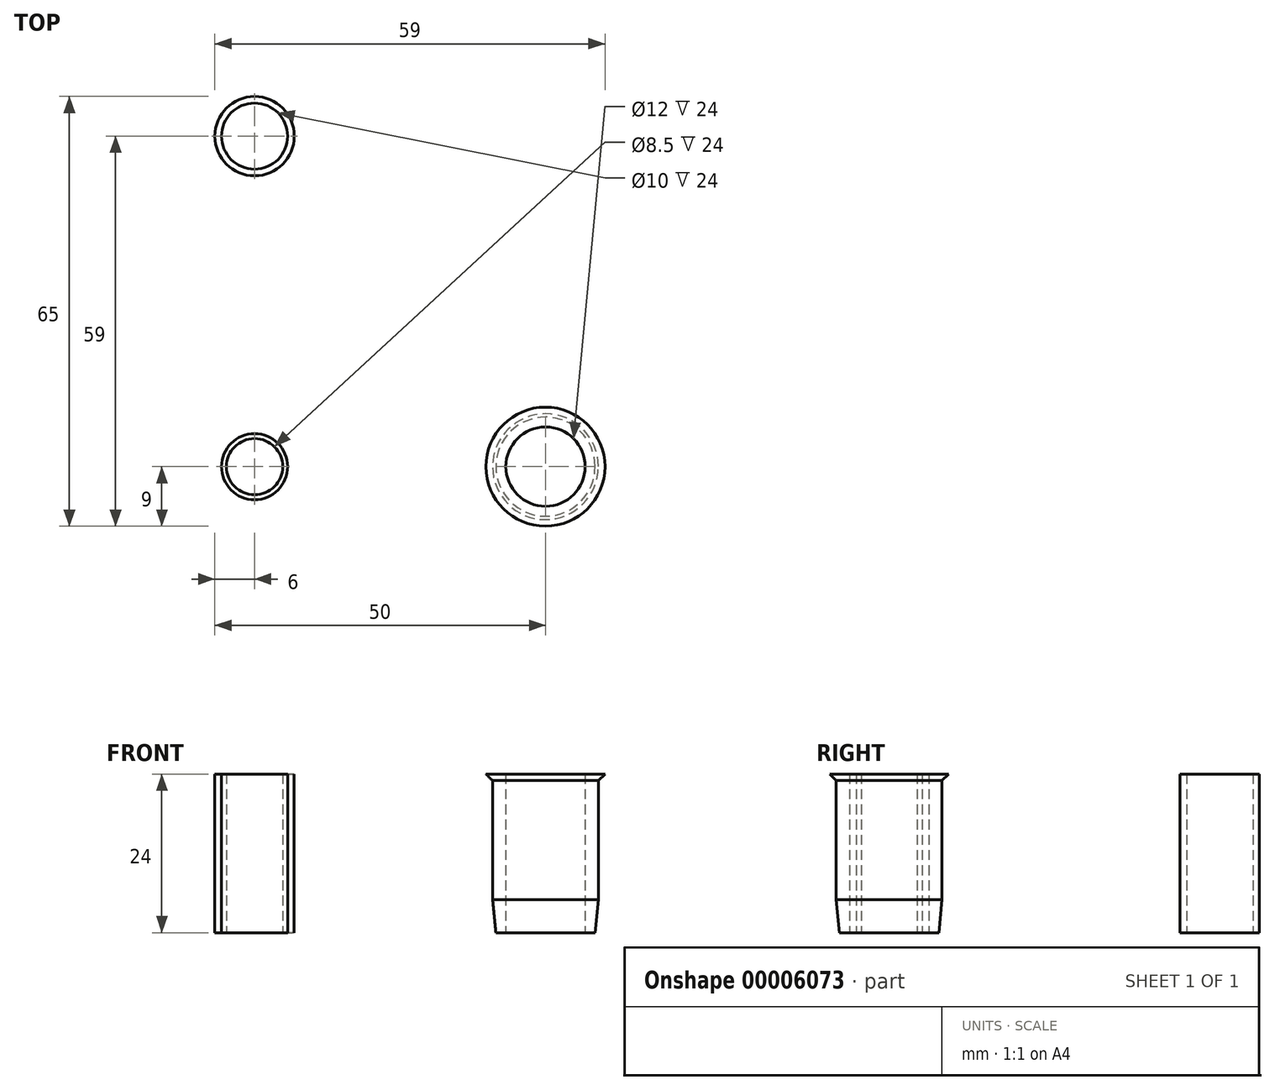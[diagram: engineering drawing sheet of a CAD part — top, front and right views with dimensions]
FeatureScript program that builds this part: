
annotation { "Feature Type Name" : "Feature", "Feature Type Description" : "" }
export const myFeature = defineFeature(function(context is Context, id is Id, definition is map)
    precondition{}
    {
        {
            var Q0;
            Q0=qCreatedBy(makeId("Top.planeOp"),FACE);
            var sketch = newSketch(context, id + "F0", { "sketchPlane" : qUnion([Q0])});
            skCircle(sketch, "E0", {"center": v(0, 0) * mm, "radius": 4.25 * mm});
            skCircle(sketch, "E1", {"center": v(0, 0) * mm, "radius": 5 * mm});
            skLineSegment(sketch, "E2.bottom", {"start": v(0, 0) * mm, "end": v(50, 0) * mm, "construction": true});
            skLineSegment(sketch, "E2.top", {"start": v(0, 50) * mm, "end": v(50, 50) * mm, "construction": true});
            skLineSegment(sketch, "E2.left", {"start": v(0, 0) * mm, "end": v(0, 50) * mm, "construction": true});
            skLineSegment(sketch, "E2.right", {"start": v(50, 0) * mm, "end": v(50, 50) * mm, "construction": true});
            skCircle(sketch, "E3", {"center": v(0, 50) * mm, "radius": 5 * mm});
            skCircle(sketch, "E4", {"center": v(0, 50) * mm, "radius": 6 * mm});
            skLineSegment(sketch, "E5.bottom", {"start": v(50, 0) * mm, "end": v(52, 0) * mm});
            skLineSegment(sketch, "E5.top", {"start": v(50, 24) * mm, "end": v(52, 24) * mm});
            skLineSegment(sketch, "E5.left", {"start": v(50, 0) * mm, "end": v(50, 24) * mm});
            skLineSegment(sketch, "E5.right", {"start": v(52, 0) * mm, "end": v(52, 24) * mm});
            skLineSegment(sketch, "E6", {"start": v(52, 24) * mm, "end": v(53, 24) * mm});
            skLineSegment(sketch, "E7", {"start": v(53, 24) * mm, "end": v(52, 23) * mm});
            skLineSegment(sketch, "E8", {"start": v(52, 23) * mm, "end": v(52, 24) * mm});
            skSolve(sketch);
        }
        {
            var Q0;
            Q0=makeQuery(id+"F0.imprint","IMPRINT",FACE,{"disambiguationData":[TD([[makeQuery(id+"F0.imprint","IMPRINT",EDGE,{"derivedFrom":sQuery(id+"F0.wireOp",EDGE,"E0")}),-1.0]])]});
            var Q1;
            Q1=makeQuery(id+"F0.imprint","IMPRINT",FACE,{"disambiguationData":[TD([[makeQuery(id+"F0.imprint","IMPRINT",EDGE,{"derivedFrom":sQuery(id+"F0.wireOp",EDGE,"E3")}),-1.0]])]});
            extrude(context, id + "F1", {"entities" : qUnion([Q0, Q1]), "depth" : 24 * mm});
        }
        {
            var Q0;
            Q0=qCreatedBy(makeId("Front.planeOp"),FACE);
            var sketch = newSketch(context, id + "F2", { "sketchPlane" : qUnion([Q0])});
            skLineSegment(sketch, "E9.bottom", {"start": v(0, 0) * mm, "end": v(50, 0) * mm, "construction": true});
            skLineSegment(sketch, "E9.top", {"start": v(0, 50) * mm, "end": v(50, 50) * mm, "construction": true});
            skLineSegment(sketch, "E9.left", {"start": v(0, 0) * mm, "end": v(0, 50) * mm, "construction": true});
            skLineSegment(sketch, "E9.right", {"start": v(50, 0) * mm, "end": v(50, 50) * mm, "construction": true});
            skLineSegment(sketch, "E10", {"start": v(50, 0) * mm, "end": v(50, 24) * mm});
            skLineSegment(sketch, "E11", {"start": v(50, 24) * mm, "end": v(53, 24) * mm});
            skLineSegment(sketch, "E12", {"start": v(53, 24) * mm, "end": v(52, 23) * mm});
            skLineSegment(sketch, "E13", {"start": v(51.5, 0) * mm, "end": v(50, 0) * mm});
            skLineSegment(sketch, "E14", {"start": v(52, 23) * mm, "end": v(52, 24) * mm, "construction": true});
            skLineSegment(sketch, "E15", {"start": v(50, 11.9) * mm, "end": v(44, 11.9) * mm, "construction": true});
            skLineSegment(sketch, "E16", {"start": v(44, 11.9) * mm, "end": v(44, 18.94) * mm, "construction": true});
            skLineSegment(sketch, "E17", {"start": v(52, 23) * mm, "end": v(52, 5) * mm});
            skLineSegment(sketch, "E18", {"start": v(52, 5) * mm, "end": v(51.5, 0) * mm});
            skSolve(sketch);
        }
        {
            var Q0;
            Q0=qSketchRegion(id+"F2",true);
            var Q1;
            Q1=sQuery(id+"F2.wireOp",EDGE,"E16");
            revolve(context, id + "F3", {"entities" : qUnion([Q0]), "axis" : qUnion([Q1]), "revolveType" : RevolveType.FULL});
        }
    });
